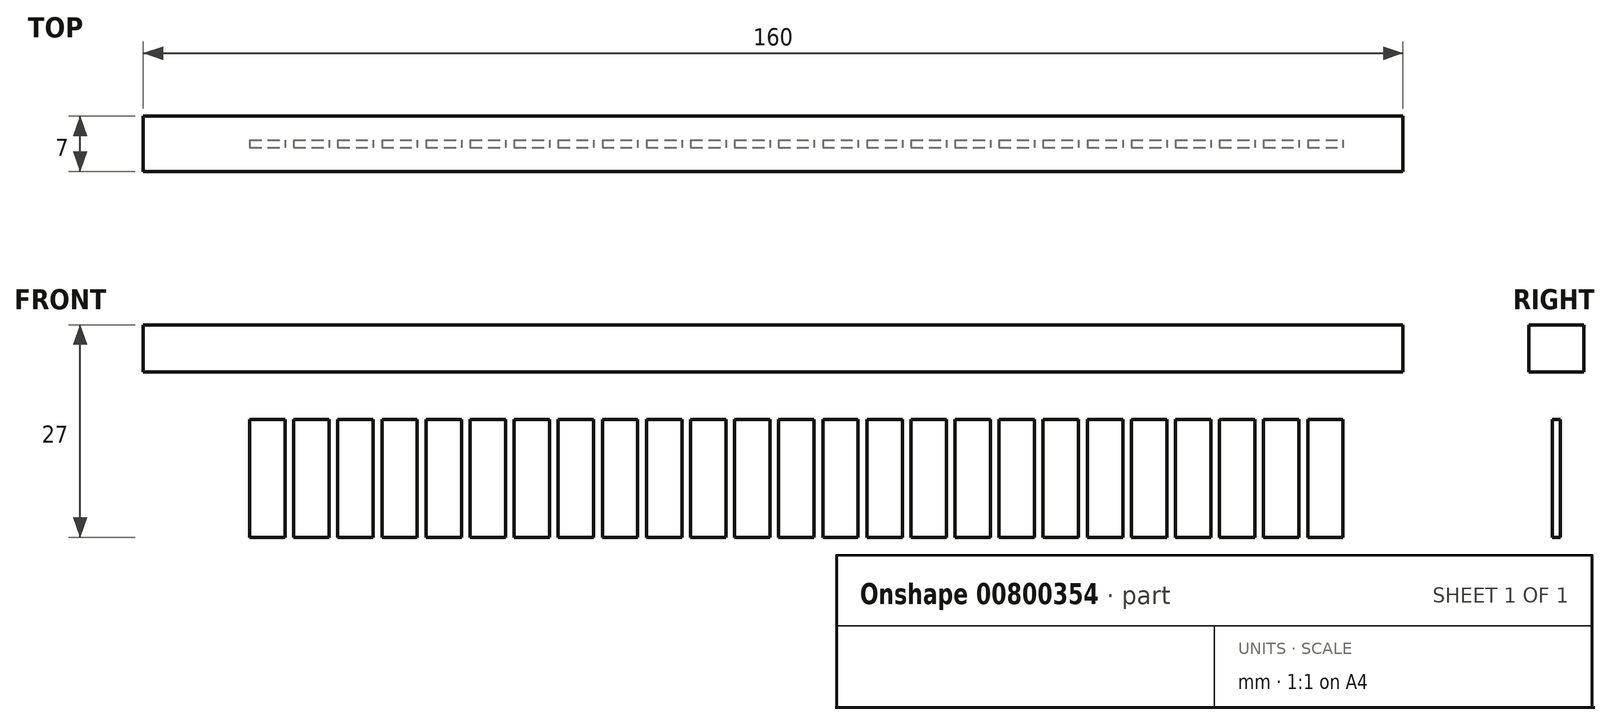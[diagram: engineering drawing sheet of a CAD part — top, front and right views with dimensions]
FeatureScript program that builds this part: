
annotation { "Feature Type Name" : "Feature", "Feature Type Description" : "" }
export const myFeature = defineFeature(function(context is Context, id is Id, definition is map)
    precondition{}
    {
        {
            var Q0;
            Q0=qCreatedBy(makeId("Front.planeOp"),FACE);
            var sketch = newSketch(context, id + "F0", { "sketchPlane" : qUnion([Q0])});
            skLineSegment(sketch, "E0.bottom", {"start": v(80, 3) * mm, "end": v(-80, 3) * mm});
            skLineSegment(sketch, "E0.top", {"start": v(80, -3) * mm, "end": v(-80, -3) * mm});
            skLineSegment(sketch, "E0.left", {"start": v(80, 3) * mm, "end": v(80, -3) * mm});
            skLineSegment(sketch, "E0.right", {"start": v(-80, 3) * mm, "end": v(-80, -3) * mm});
            skPoint(sketch, "E0.middle", {"position": v(0, 0) * mm});
            skPoint(sketch, "E1.middle", {"position": v(80, 3) * mm});
            skPoint(sketch, "E2.middle", {"position": v(0, 3) * mm});
            skLineSegment(sketch, "E3.bottom", {"start": v(-73, -3) * mm, "end": v(73, -3) * mm});
            skLineSegment(sketch, "E3.top", {"start": v(-73, -9) * mm, "end": v(73, -9) * mm});
            skLineSegment(sketch, "E3.left", {"start": v(-73, -3) * mm, "end": v(-73, -9) * mm});
            skLineSegment(sketch, "E3.right", {"start": v(73, -3) * mm, "end": v(73, -9) * mm});
            skLineSegment(sketch, "E4.bottom", {"start": v(-72.09, -9) * mm, "end": v(-67.59, -9) * mm});
            skLineSegment(sketch, "E4.top", {"start": v(-72.09, -24) * mm, "end": v(-67.59, -24) * mm});
            skLineSegment(sketch, "E4.left", {"start": v(-72.09, -9) * mm, "end": v(-72.09, -24) * mm});
            skLineSegment(sketch, "E4.right", {"start": v(-67.59, -9) * mm, "end": v(-67.59, -24) * mm});
            skLineSegment(sketch, "E5.1.0.0", {"start": v(-66.49, -9) * mm, "end": v(-66.49, -24) * mm});
            skLineSegment(sketch, "E5.1.0.1", {"start": v(-66.49, -9) * mm, "end": v(-61.99, -9) * mm});
            skLineSegment(sketch, "E5.1.0.2", {"start": v(-61.99, -9) * mm, "end": v(-61.99, -24) * mm});
            skLineSegment(sketch, "E5.1.0.3", {"start": v(-66.49, -24) * mm, "end": v(-61.99, -24) * mm});
            skLineSegment(sketch, "E5.2.0.0", {"start": v(-60.89, -9) * mm, "end": v(-60.89, -24) * mm});
            skLineSegment(sketch, "E5.2.0.1", {"start": v(-60.89, -9) * mm, "end": v(-56.39, -9) * mm});
            skLineSegment(sketch, "E5.2.0.2", {"start": v(-56.39, -9) * mm, "end": v(-56.39, -24) * mm});
            skLineSegment(sketch, "E5.2.0.3", {"start": v(-60.89, -24) * mm, "end": v(-56.39, -24) * mm});
            skLineSegment(sketch, "E5.3.0.0", {"start": v(-55.29, -9) * mm, "end": v(-55.29, -24) * mm});
            skLineSegment(sketch, "E5.3.0.1", {"start": v(-55.29, -9) * mm, "end": v(-50.79, -9) * mm});
            skLineSegment(sketch, "E5.3.0.2", {"start": v(-50.79, -9) * mm, "end": v(-50.79, -24) * mm});
            skLineSegment(sketch, "E5.3.0.3", {"start": v(-55.29, -24) * mm, "end": v(-50.79, -24) * mm});
            skLineSegment(sketch, "E5.4.0.0", {"start": v(-49.69, -9) * mm, "end": v(-49.69, -24) * mm});
            skLineSegment(sketch, "E5.4.0.1", {"start": v(-49.69, -9) * mm, "end": v(-45.19, -9) * mm});
            skLineSegment(sketch, "E5.4.0.2", {"start": v(-45.19, -9) * mm, "end": v(-45.19, -24) * mm});
            skLineSegment(sketch, "E5.4.0.3", {"start": v(-49.69, -24) * mm, "end": v(-45.19, -24) * mm});
            skLineSegment(sketch, "E5.5.0.0", {"start": v(-44.09, -9) * mm, "end": v(-44.09, -24) * mm});
            skLineSegment(sketch, "E5.5.0.1", {"start": v(-44.09, -9) * mm, "end": v(-39.59, -9) * mm});
            skLineSegment(sketch, "E5.5.0.2", {"start": v(-39.59, -9) * mm, "end": v(-39.59, -24) * mm});
            skLineSegment(sketch, "E5.5.0.3", {"start": v(-44.09, -24) * mm, "end": v(-39.59, -24) * mm});
            skLineSegment(sketch, "E5.6.0.0", {"start": v(-38.49, -9) * mm, "end": v(-38.49, -24) * mm});
            skLineSegment(sketch, "E5.6.0.1", {"start": v(-38.49, -9) * mm, "end": v(-33.99, -9) * mm});
            skLineSegment(sketch, "E5.6.0.2", {"start": v(-33.99, -9) * mm, "end": v(-33.99, -24) * mm});
            skLineSegment(sketch, "E5.6.0.3", {"start": v(-38.49, -24) * mm, "end": v(-33.99, -24) * mm});
            skLineSegment(sketch, "E5.7.0.0", {"start": v(-32.89, -9) * mm, "end": v(-32.89, -24) * mm});
            skLineSegment(sketch, "E5.7.0.1", {"start": v(-32.89, -9) * mm, "end": v(-28.39, -9) * mm});
            skLineSegment(sketch, "E5.7.0.2", {"start": v(-28.39, -9) * mm, "end": v(-28.39, -24) * mm});
            skLineSegment(sketch, "E5.7.0.3", {"start": v(-32.89, -24) * mm, "end": v(-28.39, -24) * mm});
            skLineSegment(sketch, "E5.8.0.0", {"start": v(-27.29, -9) * mm, "end": v(-27.29, -24) * mm});
            skLineSegment(sketch, "E5.8.0.1", {"start": v(-27.29, -9) * mm, "end": v(-22.79, -9) * mm});
            skLineSegment(sketch, "E5.8.0.2", {"start": v(-22.79, -9) * mm, "end": v(-22.79, -24) * mm});
            skLineSegment(sketch, "E5.8.0.3", {"start": v(-27.29, -24) * mm, "end": v(-22.79, -24) * mm});
            skLineSegment(sketch, "E5.9.0.0", {"start": v(-21.69, -9) * mm, "end": v(-21.69, -24) * mm});
            skLineSegment(sketch, "E5.9.0.1", {"start": v(-21.69, -9) * mm, "end": v(-17.19, -9) * mm});
            skLineSegment(sketch, "E5.9.0.2", {"start": v(-17.19, -9) * mm, "end": v(-17.19, -24) * mm});
            skLineSegment(sketch, "E5.9.0.3", {"start": v(-21.69, -24) * mm, "end": v(-17.19, -24) * mm});
            skLineSegment(sketch, "E5.10.0.0", {"start": v(-16.09, -9) * mm, "end": v(-16.09, -24) * mm});
            skLineSegment(sketch, "E5.10.0.1", {"start": v(-16.09, -9) * mm, "end": v(-11.59, -9) * mm});
            skLineSegment(sketch, "E5.10.0.2", {"start": v(-11.59, -9) * mm, "end": v(-11.59, -24) * mm});
            skLineSegment(sketch, "E5.10.0.3", {"start": v(-16.09, -24) * mm, "end": v(-11.59, -24) * mm});
            skLineSegment(sketch, "E5.11.0.0", {"start": v(-10.49, -9) * mm, "end": v(-10.49, -24) * mm});
            skLineSegment(sketch, "E5.11.0.1", {"start": v(-10.49, -9) * mm, "end": v(-5.99, -9) * mm});
            skLineSegment(sketch, "E5.11.0.2", {"start": v(-5.99, -9) * mm, "end": v(-5.99, -24) * mm});
            skLineSegment(sketch, "E5.11.0.3", {"start": v(-10.49, -24) * mm, "end": v(-5.99, -24) * mm});
            skLineSegment(sketch, "E5.12.0.0", {"start": v(-4.89, -9) * mm, "end": v(-4.89, -24) * mm});
            skLineSegment(sketch, "E5.12.0.1", {"start": v(-4.89, -9) * mm, "end": v(-0.39, -9) * mm});
            skLineSegment(sketch, "E5.12.0.2", {"start": v(-0.39, -9) * mm, "end": v(-0.39, -24) * mm});
            skLineSegment(sketch, "E5.12.0.3", {"start": v(-4.89, -24) * mm, "end": v(-0.39, -24) * mm});
            skLineSegment(sketch, "E5.13.0.0", {"start": v(0.71, -9) * mm, "end": v(0.71, -24) * mm});
            skLineSegment(sketch, "E5.13.0.1", {"start": v(0.71, -9) * mm, "end": v(5.21, -9) * mm});
            skLineSegment(sketch, "E5.13.0.2", {"start": v(5.21, -9) * mm, "end": v(5.21, -24) * mm});
            skLineSegment(sketch, "E5.13.0.3", {"start": v(0.71, -24) * mm, "end": v(5.21, -24) * mm});
            skLineSegment(sketch, "E5.14.0.0", {"start": v(6.31, -9) * mm, "end": v(6.31, -24) * mm});
            skLineSegment(sketch, "E5.14.0.1", {"start": v(6.31, -9) * mm, "end": v(10.81, -9) * mm});
            skLineSegment(sketch, "E5.14.0.2", {"start": v(10.81, -9) * mm, "end": v(10.81, -24) * mm});
            skLineSegment(sketch, "E5.14.0.3", {"start": v(6.31, -24) * mm, "end": v(10.81, -24) * mm});
            skLineSegment(sketch, "E5.15.0.0", {"start": v(11.91, -9) * mm, "end": v(11.91, -24) * mm});
            skLineSegment(sketch, "E5.15.0.1", {"start": v(11.91, -9) * mm, "end": v(16.41, -9) * mm});
            skLineSegment(sketch, "E5.15.0.2", {"start": v(16.41, -9) * mm, "end": v(16.41, -24) * mm});
            skLineSegment(sketch, "E5.15.0.3", {"start": v(11.91, -24) * mm, "end": v(16.41, -24) * mm});
            skLineSegment(sketch, "E5.16.0.0", {"start": v(17.51, -9) * mm, "end": v(17.51, -24) * mm});
            skLineSegment(sketch, "E5.16.0.1", {"start": v(17.51, -9) * mm, "end": v(22.01, -9) * mm});
            skLineSegment(sketch, "E5.16.0.2", {"start": v(22.01, -9) * mm, "end": v(22.01, -24) * mm});
            skLineSegment(sketch, "E5.16.0.3", {"start": v(17.51, -24) * mm, "end": v(22.01, -24) * mm});
            skLineSegment(sketch, "E5.17.0.0", {"start": v(23.11, -9) * mm, "end": v(23.11, -24) * mm});
            skLineSegment(sketch, "E5.17.0.1", {"start": v(23.11, -9) * mm, "end": v(27.61, -9) * mm});
            skLineSegment(sketch, "E5.17.0.2", {"start": v(27.61, -9) * mm, "end": v(27.61, -24) * mm});
            skLineSegment(sketch, "E5.17.0.3", {"start": v(23.11, -24) * mm, "end": v(27.61, -24) * mm});
            skLineSegment(sketch, "E5.18.0.0", {"start": v(28.71, -9) * mm, "end": v(28.71, -24) * mm});
            skLineSegment(sketch, "E5.18.0.1", {"start": v(28.71, -9) * mm, "end": v(33.21, -9) * mm});
            skLineSegment(sketch, "E5.18.0.2", {"start": v(33.21, -9) * mm, "end": v(33.21, -24) * mm});
            skLineSegment(sketch, "E5.18.0.3", {"start": v(28.71, -24) * mm, "end": v(33.21, -24) * mm});
            skLineSegment(sketch, "E5.19.0.0", {"start": v(34.31, -9) * mm, "end": v(34.31, -24) * mm});
            skLineSegment(sketch, "E5.19.0.1", {"start": v(34.31, -9) * mm, "end": v(38.81, -9) * mm});
            skLineSegment(sketch, "E5.19.0.2", {"start": v(38.81, -9) * mm, "end": v(38.81, -24) * mm});
            skLineSegment(sketch, "E5.19.0.3", {"start": v(34.31, -24) * mm, "end": v(38.81, -24) * mm});
            skLineSegment(sketch, "E5.20.0.0", {"start": v(39.91, -9) * mm, "end": v(39.91, -24) * mm});
            skLineSegment(sketch, "E5.20.0.1", {"start": v(39.91, -9) * mm, "end": v(44.41, -9) * mm});
            skLineSegment(sketch, "E5.20.0.2", {"start": v(44.41, -9) * mm, "end": v(44.41, -24) * mm});
            skLineSegment(sketch, "E5.20.0.3", {"start": v(39.91, -24) * mm, "end": v(44.41, -24) * mm});
            skLineSegment(sketch, "E5.21.0.0", {"start": v(45.51, -9) * mm, "end": v(45.51, -24) * mm});
            skLineSegment(sketch, "E5.21.0.1", {"start": v(45.51, -9) * mm, "end": v(50.01, -9) * mm});
            skLineSegment(sketch, "E5.21.0.2", {"start": v(50.01, -9) * mm, "end": v(50.01, -24) * mm});
            skLineSegment(sketch, "E5.21.0.3", {"start": v(45.51, -24) * mm, "end": v(50.01, -24) * mm});
            skLineSegment(sketch, "E5.22.0.0", {"start": v(51.11, -9) * mm, "end": v(51.11, -24) * mm});
            skLineSegment(sketch, "E5.22.0.1", {"start": v(51.11, -9) * mm, "end": v(55.61, -9) * mm});
            skLineSegment(sketch, "E5.22.0.2", {"start": v(55.61, -9) * mm, "end": v(55.61, -24) * mm});
            skLineSegment(sketch, "E5.22.0.3", {"start": v(51.11, -24) * mm, "end": v(55.61, -24) * mm});
            skLineSegment(sketch, "E5.23.0.0", {"start": v(56.71, -9) * mm, "end": v(56.71, -24) * mm});
            skLineSegment(sketch, "E5.23.0.1", {"start": v(56.71, -9) * mm, "end": v(61.21, -9) * mm});
            skLineSegment(sketch, "E5.23.0.2", {"start": v(61.21, -9) * mm, "end": v(61.21, -24) * mm});
            skLineSegment(sketch, "E5.23.0.3", {"start": v(56.71, -24) * mm, "end": v(61.21, -24) * mm});
            skLineSegment(sketch, "E5.24.0.0", {"start": v(62.31, -9) * mm, "end": v(62.31, -24) * mm});
            skLineSegment(sketch, "E5.24.0.1", {"start": v(62.31, -9) * mm, "end": v(66.81, -9) * mm});
            skLineSegment(sketch, "E5.24.0.2", {"start": v(66.81, -9) * mm, "end": v(66.81, -24) * mm});
            skLineSegment(sketch, "E5.24.0.3", {"start": v(62.31, -24) * mm, "end": v(66.81, -24) * mm});
            skLineSegment(sketch, "E5.25.0.0", {"start": v(67.91, -9) * mm, "end": v(67.91, -24) * mm});
            skLineSegment(sketch, "E5.25.0.1", {"start": v(67.91, -9) * mm, "end": v(72.41, -9) * mm});
            skLineSegment(sketch, "E5.25.0.2", {"start": v(72.41, -9) * mm, "end": v(72.41, -24) * mm});
            skLineSegment(sketch, "E5.25.0.3", {"start": v(67.91, -24) * mm, "end": v(72.41, -24) * mm});
            skLineSegment(sketch, "E5.direction1", {"start": v(-72.09, -24) * mm, "end": v(-66.49, -24) * mm, "construction": true});
            skSolve(sketch);
        }
        {
            var Q0;
            Q0=makeQuery(id+"F0.imprint","IMPRINT",FACE,{"disambiguationData":[TD([[makeQuery(id+"F0.imprint","IMPRINT",EDGE,{"derivedFrom":sQuery(id+"F0.wireOp",EDGE,"E5.25.0.0")}),1.0]])]});
            var Q1;
            Q1=makeQuery(id+"F0.imprint","IMPRINT",FACE,{"disambiguationData":[TD([[makeQuery(id+"F0.imprint","IMPRINT",EDGE,{"derivedFrom":sQuery(id+"F0.wireOp",EDGE,"E5.22.0.0")}),1.0]])]});
            var Q2;
            Q2=makeQuery(id+"F0.imprint","IMPRINT",FACE,{"disambiguationData":[TD([[makeQuery(id+"F0.imprint","IMPRINT",EDGE,{"derivedFrom":sQuery(id+"F0.wireOp",EDGE,"E5.23.0.0")}),1.0]])]});
            var Q3;
            Q3=makeQuery(id+"F0.imprint","IMPRINT",FACE,{"disambiguationData":[TD([[makeQuery(id+"F0.imprint","IMPRINT",EDGE,{"derivedFrom":sQuery(id+"F0.wireOp",EDGE,"E5.16.0.0")}),1.0]])]});
            var Q4;
            Q4=makeQuery(id+"F0.imprint","IMPRINT",FACE,{"disambiguationData":[TD([[makeQuery(id+"F0.imprint","IMPRINT",EDGE,{"derivedFrom":sQuery(id+"F0.wireOp",EDGE,"E5.24.0.0")}),1.0]])]});
            var Q5;
            Q5=makeQuery(id+"F0.imprint","IMPRINT",FACE,{"disambiguationData":[TD([[makeQuery(id+"F0.imprint","IMPRINT",EDGE,{"derivedFrom":sQuery(id+"F0.wireOp",EDGE,"E5.17.0.0")}),1.0]])]});
            var Q6;
            Q6=makeQuery(id+"F0.imprint","IMPRINT",FACE,{"disambiguationData":[TD([[makeQuery(id+"F0.imprint","IMPRINT",EDGE,{"derivedFrom":sQuery(id+"F0.wireOp",EDGE,"E5.11.0.0")}),1.0]])]});
            var Q7;
            Q7=makeQuery(id+"F0.imprint","IMPRINT",FACE,{"disambiguationData":[TD([[makeQuery(id+"F0.imprint","IMPRINT",EDGE,{"derivedFrom":sQuery(id+"F0.wireOp",EDGE,"E5.10.0.0")}),1.0]])]});
            var Q8;
            Q8=makeQuery(id+"F0.imprint","IMPRINT",FACE,{"disambiguationData":[TD([[makeQuery(id+"F0.imprint","IMPRINT",EDGE,{"derivedFrom":sQuery(id+"F0.wireOp",EDGE,"E5.9.0.0")}),1.0]])]});
            var Q9;
            Q9=makeQuery(id+"F0.imprint","IMPRINT",FACE,{"disambiguationData":[TD([[makeQuery(id+"F0.imprint","IMPRINT",EDGE,{"derivedFrom":sQuery(id+"F0.wireOp",EDGE,"E5.7.0.0")}),1.0]])]});
            var Q10;
            Q10=makeQuery(id+"F0.imprint","IMPRINT",FACE,{"disambiguationData":[TD([[makeQuery(id+"F0.imprint","IMPRINT",EDGE,{"derivedFrom":sQuery(id+"F0.wireOp",EDGE,"E5.8.0.0")}),1.0]])]});
            var Q11;
            Q11=makeQuery(id+"F0.imprint","IMPRINT",FACE,{"disambiguationData":[TD([[makeQuery(id+"F0.imprint","IMPRINT",EDGE,{"derivedFrom":sQuery(id+"F0.wireOp",EDGE,"E5.6.0.0")}),1.0]])]});
            var Q12;
            Q12=makeQuery(id+"F0.imprint","IMPRINT",FACE,{"disambiguationData":[TD([[makeQuery(id+"F0.imprint","IMPRINT",EDGE,{"derivedFrom":sQuery(id+"F0.wireOp",EDGE,"E5.5.0.0")}),1.0]])]});
            var Q13;
            Q13=makeQuery(id+"F0.imprint","IMPRINT",FACE,{"disambiguationData":[TD([[makeQuery(id+"F0.imprint","IMPRINT",EDGE,{"derivedFrom":sQuery(id+"F0.wireOp",EDGE,"E5.4.0.0")}),1.0]])]});
            var Q14;
            Q14=makeQuery(id+"F0.imprint","IMPRINT",FACE,{"disambiguationData":[TD([[makeQuery(id+"F0.imprint","IMPRINT",EDGE,{"derivedFrom":sQuery(id+"F0.wireOp",EDGE,"E5.3.0.0")}),1.0]])]});
            var Q15;
            Q15=makeQuery(id+"F0.imprint","IMPRINT",FACE,{"disambiguationData":[TD([[makeQuery(id+"F0.imprint","IMPRINT",EDGE,{"derivedFrom":sQuery(id+"F0.wireOp",EDGE,"E5.2.0.0")}),1.0]])]});
            var Q16;
            Q16=makeQuery(id+"F0.imprint","IMPRINT",FACE,{"disambiguationData":[TD([[makeQuery(id+"F0.imprint","IMPRINT",EDGE,{"derivedFrom":sQuery(id+"F0.wireOp",EDGE,"E5.1.0.0")}),1.0]])]});
            var Q17;
            Q17=makeQuery(id+"F0.imprint","IMPRINT",FACE,{"disambiguationData":[TD([[makeQuery(id+"F0.imprint","IMPRINT",EDGE,{"derivedFrom":sQuery(id+"F0.wireOp",EDGE,"E4.bottom")}),-1.0]])]});
            var Q18;
            Q18=makeQuery(id+"F0.imprint","IMPRINT",FACE,{"disambiguationData":[TD([[makeQuery(id+"F0.imprint","IMPRINT",EDGE,{"derivedFrom":sQuery(id+"F0.wireOp",EDGE,"E5.15.0.0")}),1.0]])]});
            var Q19;
            Q19=makeQuery(id+"F0.imprint","IMPRINT",FACE,{"disambiguationData":[TD([[makeQuery(id+"F0.imprint","IMPRINT",EDGE,{"derivedFrom":sQuery(id+"F0.wireOp",EDGE,"E5.13.0.0")}),1.0]])]});
            var Q20;
            Q20=makeQuery(id+"F0.imprint","IMPRINT",FACE,{"disambiguationData":[TD([[makeQuery(id+"F0.imprint","IMPRINT",EDGE,{"derivedFrom":sQuery(id+"F0.wireOp",EDGE,"E5.12.0.0")}),1.0]])]});
            var Q21;
            Q21=makeQuery(id+"F0.imprint","IMPRINT",FACE,{"disambiguationData":[TD([[makeQuery(id+"F0.imprint","IMPRINT",EDGE,{"derivedFrom":sQuery(id+"F0.wireOp",EDGE,"E5.14.0.0")}),1.0]])]});
            var Q22;
            Q22=makeQuery(id+"F0.imprint","IMPRINT",FACE,{"disambiguationData":[TD([[makeQuery(id+"F0.imprint","IMPRINT",EDGE,{"derivedFrom":sQuery(id+"F0.wireOp",EDGE,"E5.21.0.0")}),1.0]])]});
            var Q23;
            Q23=makeQuery(id+"F0.imprint","IMPRINT",FACE,{"disambiguationData":[TD([[makeQuery(id+"F0.imprint","IMPRINT",EDGE,{"derivedFrom":sQuery(id+"F0.wireOp",EDGE,"E5.20.0.0")}),1.0]])]});
            var Q24;
            Q24=makeQuery(id+"F0.imprint","IMPRINT",FACE,{"disambiguationData":[TD([[makeQuery(id+"F0.imprint","IMPRINT",EDGE,{"derivedFrom":sQuery(id+"F0.wireOp",EDGE,"E5.19.0.0")}),1.0]])]});
            var Q25;
            Q25=makeQuery(id+"F0.imprint","IMPRINT",FACE,{"disambiguationData":[TD([[makeQuery(id+"F0.imprint","IMPRINT",EDGE,{"derivedFrom":sQuery(id+"F0.wireOp",EDGE,"E5.18.0.0")}),1.0]])]});
            extrude(context, id + "F1", {"entities" : qUnion([Q0, Q1, Q2, Q3, Q4, Q5, Q6, Q7, Q8, Q9, Q10, Q11, Q12, Q13, Q14, Q15, Q16, Q17, Q18, Q19, Q20, Q21, Q22, Q23, Q24, Q25]), "endBound" : BoundingType.SYMMETRIC, "oppositeDirection" : true, "depth" : 1 * mm, "offsetDistance" : 25.4 * mm});
        }
        {
            var Q0;
            Q0=makeQuery(id+"F0.imprint","IMPRINT",FACE,{"disambiguationData":[TD([[makeQuery(id+"F0.imprint","IMPRINT",EDGE,{"derivedFrom":sQuery(id+"F0.wireOp",EDGE,"E0.bottom")}),1.0]])]});
            var Q1;
            Q1=makeQuery(id+"F0.imprint","IMPRINT",FACE,{"disambiguationData":[TD([[makeQuery(id+"F0.imprint","IMPRINT",EDGE,{"derivedFrom":sQuery(id+"F0.wireOp",EDGE,"E3.bottom")}),-1.0]])]});
            extrude(context, id + "F2", {"entities" : qUnion([Q0, Q1]), "endBound" : BoundingType.SYMMETRIC, "depth" : 7 * mm, "offsetDistance" : 25.4 * mm});
        }
    });
